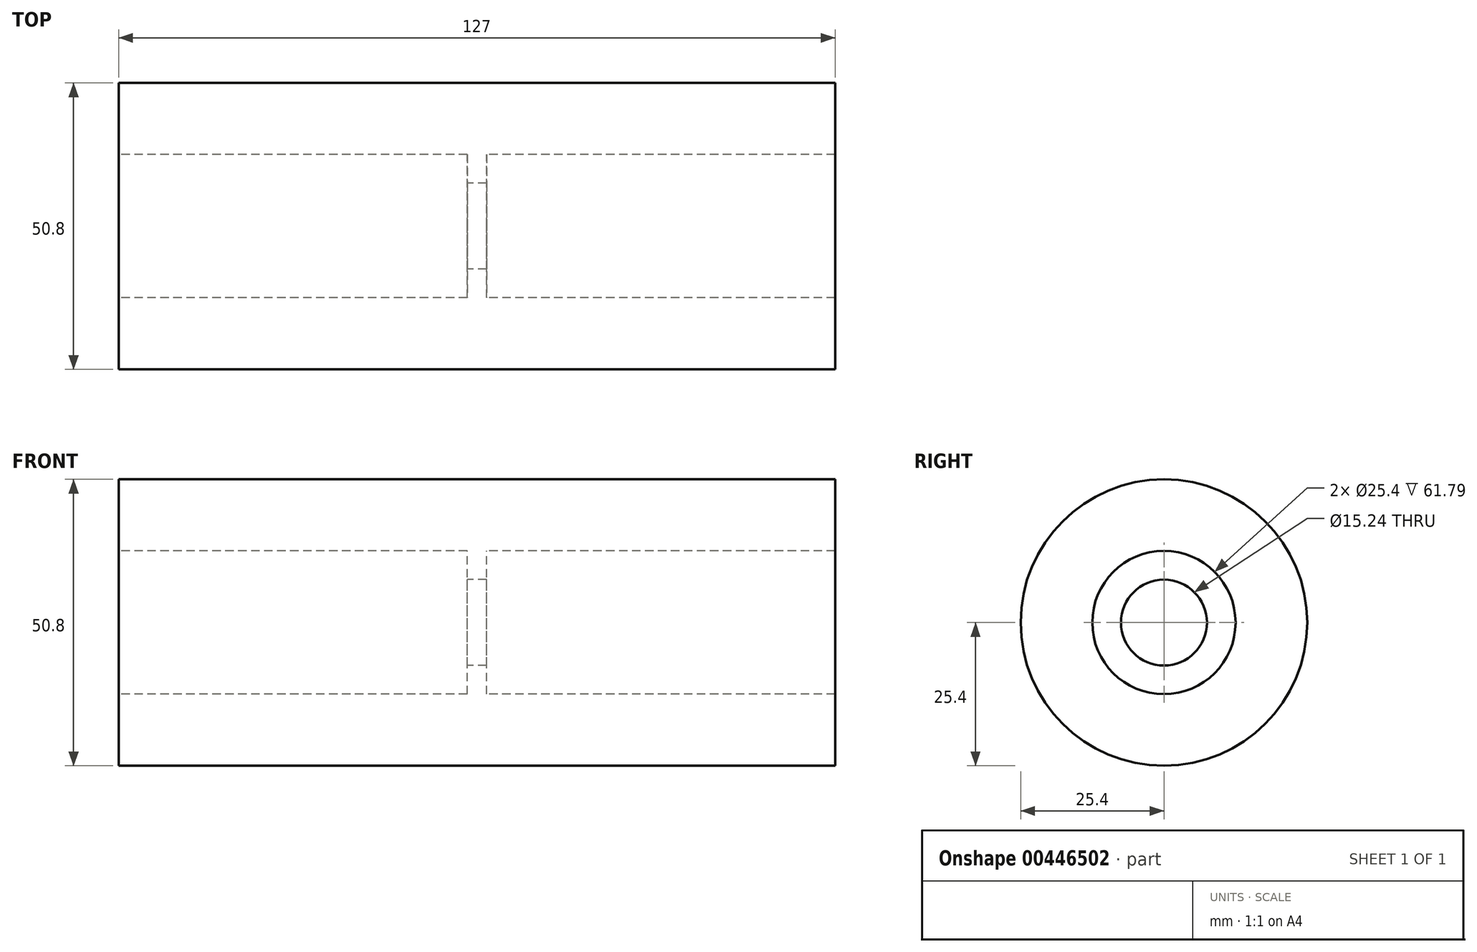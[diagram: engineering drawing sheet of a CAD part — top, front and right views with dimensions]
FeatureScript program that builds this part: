
annotation { "Feature Type Name" : "Feature", "Feature Type Description" : "" }
export const myFeature = defineFeature(function(context is Context, id is Id, definition is map)
    precondition{}
    {
        {
            var Q0;
            Q0=qCreatedBy(makeId("Right.planeOp"),FACE);
            var sketch = newSketch(context, id + "F0", { "sketchPlane" : qUnion([Q0])});
            skCircle(sketch, "E0", {"center": v(0, 0) * mm, "radius": 25.4 * mm});
            skCircle(sketch, "E1", {"center": v(0, 0) * mm, "radius": 12.7 * mm});
            skCircle(sketch, "E2", {"center": v(0, 0) * mm, "radius": 7.62 * mm});
            skSolve(sketch);
        }
        {
            var Q0;
            Q0=makeQuery(id+"F0.imprint","IMPRINT",FACE,{"disambiguationData":[TD([[makeQuery(id+"F0.imprint","IMPRINT",EDGE,{"derivedFrom":sQuery(id+"F0.wireOp",EDGE,"E0")}),1.0]])]});
            extrude(context, id + "F1", {"entities" : qUnion([Q0]), "depth" : 127 * mm, "symmetric" : true});
        }
        {
            var Q0;
            Q0=makeQuery(id+"F0.imprint","IMPRINT",FACE,{"disambiguationData":[TD([[makeQuery(id+"F0.imprint","IMPRINT",EDGE,{"derivedFrom":sQuery(id+"F0.wireOp",EDGE,"E1")}),1.0]])]});
            extrude(context, id + "F2", {"entities" : qUnion([Q0]), "operationType" : NewBodyOperationType.ADD, "depth" : (5 - (2 * .79)) * mm, "symmetric" : true});
        }
    });
